# Revit family: PRESTO ALPA 90 ARTE con valvula de vaciado-antivandalico
name_source: partatom
category: Aparatos sanitarios
revit_build: Autodesk Revit 2015 (Build: 20140223_1515(x64)
units: mm (PartAtom-declared; Revit-internal decimal feet)

## types (1)
- 98929
    Accionamiento = Por pulsador
    CAUDAL = 8 L/Min
    CIERRE = Automático en 30 seg.
    Comentarios de tipo = Cabeza intercambiable que comprende todo el cuerpo del grifo
Cuerpo y pulsador de latón cromado,piezas interiores en materiales que soportan hasta los 70ºC que permiten desinfecciones térmicas anti-legionela. Válvulas antirretorno incorporadas.
    Conexión AC = Sí
    Conexión AF = Sí
    Código de montaje = C1030220
    Descripción = Conjunto suministrado con grifo PRESTO ALPA 90 ARTE, regulador automático de caudal, tubo brida, con racor y rociador antivandálico orientable en latón cromado y pulsador ARTE cromado.
    ENTRADA = Macho y hembra 3/4"
    Elevación por defecto = 1219 mm
    Fabricante = PRESTO IBÉRICA
    Imagen de tipo = <Ninguno>
    Material = LATON CROMADO
    Modelo = CONJUNTO ALPA 90 ARTE CON ROCIADOR ANTIVANDALICO
    PESO BRUTO = 1.030 Kg
    REFERENCIA = 98929
    TIPO DE AGUA = Fria/Caliente
    Teléfono = (+34) 915 782 575
    URL = http://www.prestoiberica.com
